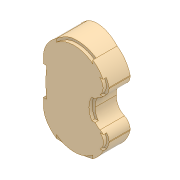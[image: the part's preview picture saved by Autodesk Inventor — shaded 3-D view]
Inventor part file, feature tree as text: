
AUTODESK INVENTOR PART (.ipt)
format: ipt  version: 2017 (Build 210142000, 142)  size: 346,112 bytes
history: native  units: mm
features: sketch x11, other x8, extrude x5, loft x2
ambient origin geometry x8: Origin, YZ Plane, XZ Plane, XY Plane, X Axis, Y Axis, Z Axis, Center Point
bodies: Body1 (feature_tree)
feature tree (26):
  other  "Bryła1"
  sketch  "Szkic1"
  extrude  "Wyciągnięcie proste1"  Depth=2.0mm TaperAngle=0.0deg
  extrude  "Wyciągnięcie proste2"  Depth=17.0mm TaperAngle=0.0deg
  other  "Płaszczyzna konstrukcyjna1"
  sketch  "Szkic5"
  sketch  "Szkic6"
  other  "Płaszczyzna konstrukcyjna3"
  sketch  "Szkic8"
  other  "Płaszczyzna konstrukcyjna4"
  other  "Płaszczyzna konstrukcyjna5"
  loft  "Wyciągnięcie złożone1"
  extrude  "Wyciągnięcie proste3"  Depth=2.0mm
  extrude  "Wyciągnięcie proste4"  Depth=13.0mm
  loft  "Wyciągnięcie złożone2"
  sketch  "Szkic19"
  sketch  "Szkic20"
  extrude  "Wyciągnięcie proste5"  Depth=14.0mm
  sketch  "Szkic10"
  sketch  "Szkic15"
  other  "Krawędzie1"
  sketch  "Szkic16"
  sketch  "Szkic17"
  sketch  "Szkic18"
  other  "Krawędzie2"
  other  "Krawędzie3"
